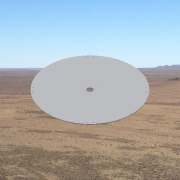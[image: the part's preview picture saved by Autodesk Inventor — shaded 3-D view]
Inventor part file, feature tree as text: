
AUTODESK INVENTOR PART (.ipt)
format: ipt  version: 2014 SP1 (Build 180222100, 222)  size: 204,800 bytes
history: native  units: in
note: dims shown in document units (in); Inventor stores cm internally (conversion verified against a paired STEP export)
features: sketch x7, hole x5, pattern_circular x5, extrude x2
ambient origin geometry x8: Origin, YZ Plane, XZ Plane, XY Plane, X Axis, Y Axis, Z Axis, Center Point
bodies: Body1 (feature_tree)
feature tree (19):
  extrude  "Extrusion1"  Depth=0.125in TaperAngle=0.0deg
  extrude  "Extrusion2"  Depth=0.125in TaperAngle=0.0deg
  hole  "Hole1"  [1 undecoded]
  pattern_circular  "Circular Pattern1"  [2 undecoded]
  hole  "Hole2"  [1 undecoded]
  pattern_circular  "Circular Pattern2"  [2 undecoded]
  hole  "Hole3"  [1 undecoded]
  pattern_circular  "Circular Pattern3"  [2 undecoded]
  hole  "Hole4"  [1 undecoded]
  pattern_circular  "Circular Pattern4"  Count=4 Angle=360.0deg
  hole  "Hole5"  [1 undecoded]
  pattern_circular  "Circular Pattern5"  Count=4 Angle=360.0deg
  sketch  "Sketch1"  dims[d0=24.0in d1=0.125in d2=0.0in]
  sketch  "Sketch2"  dims[d3=1.5in d4=0.125in d5=0.0in]
  sketch  "Sketch3"  dims[d6=11.5in]
  sketch  "Sketch4"  dims[d7=0.177in d8=0.2362in d9=0.332in d10=0.0787in d11=0.5635in d12=0.315in d13=0.8108in d14=1.5748in d15=360.0deg]
  sketch  "Sketch5"  dims[d20=11.5in]
  sketch  "Sketch6"  dims[d21=45.0deg]
  sketch  "Sketch7"  dims[d22=0.719in d23=0.719in d24=0.177in d25=0.2362in d26=0.332in d27=0.0787in d28=0.5635in d29=0.315in d30=0.8108in d31=1.5748in d32=360.0deg d34=0.875in d35=0.096in d36=0.2362in d37=0.172in d38=0.0787in d39=0.5635in d40=0.315in d41=0.8108in d42=1.5748in d43=360.0deg d46=1.125in d47=45.0deg d48=0.1285in d49=0.2362in d50=0.225in d51=0.0787in d52=0.5635in d53=0.315in d54=0.8108in d55=1.5748in d56=360.0deg d60=2.25in d61=0.1495in d62=0.2362in d63=0.279in d64=0.0787in d65=0.5635in d66=0.315in d67=0.8108in d68=1.5748in d69=360.0deg]
note: 11 required parameter values undecoded (feature->parameter linkage not recoverable at this tier; creation-order binding heuristic only, values carry confidence <= 0.55)
